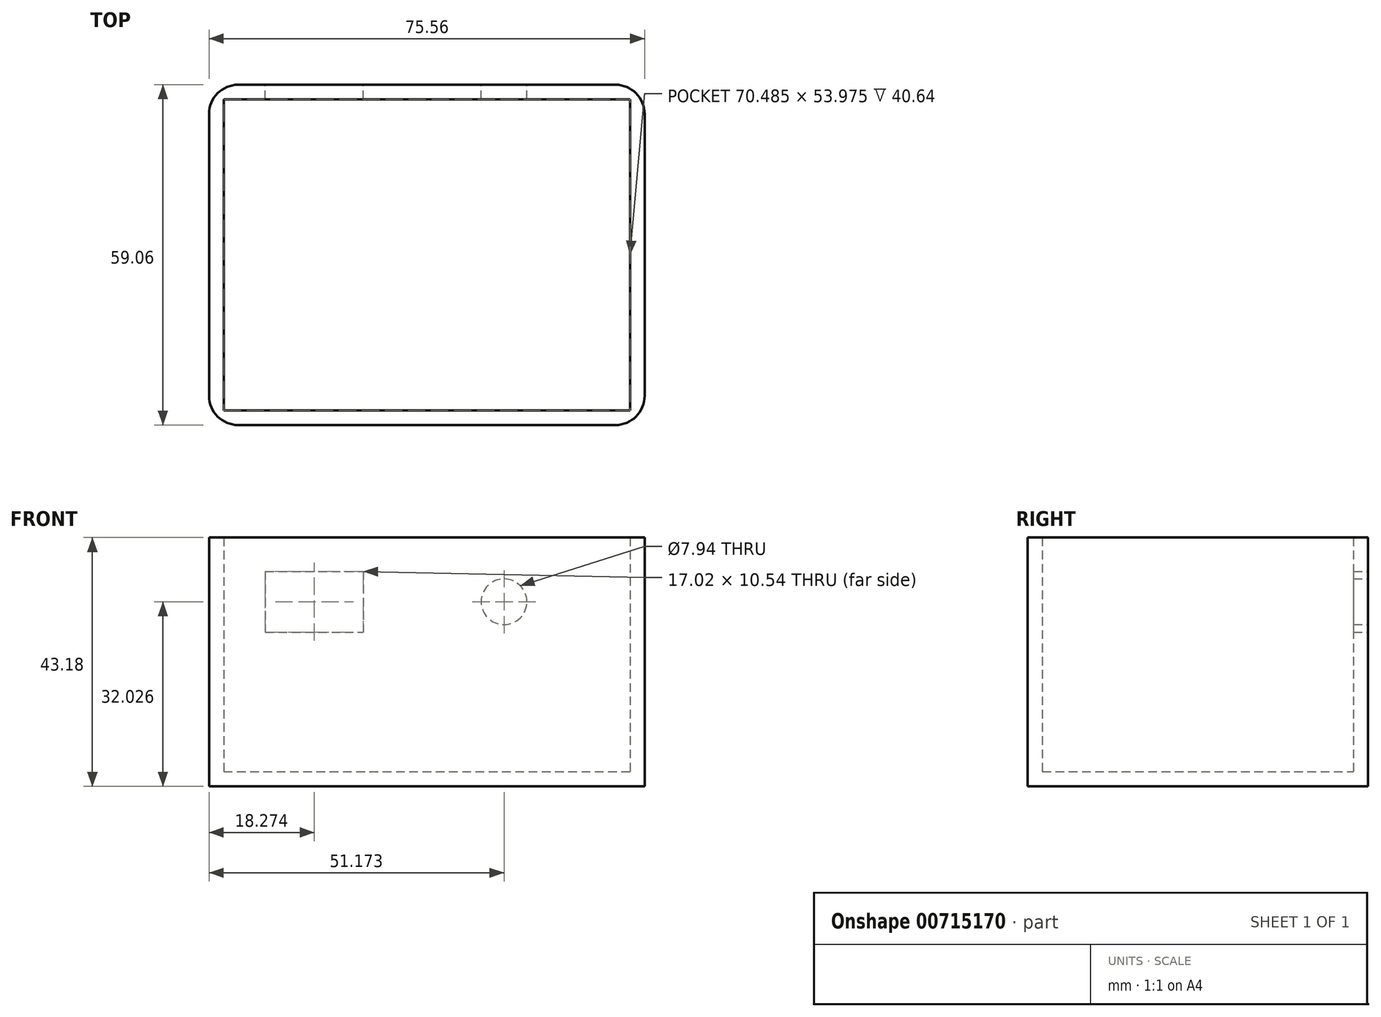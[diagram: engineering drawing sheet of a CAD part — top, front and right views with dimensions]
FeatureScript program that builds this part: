
annotation { "Feature Type Name" : "Feature", "Feature Type Description" : "" }
export const myFeature = defineFeature(function(context is Context, id is Id, definition is map)
    precondition{}
    {
        {
            var Q0;
            Q0=qCreatedBy(makeId("Top.planeOp"),FACE);
            var sketch = newSketch(context, id + "F0", { "sketchPlane" : qUnion([Q0])});
            skLineSegment(sketch, "E0.bottom", {"start": v(-37.78, -29.53) * mm, "end": v(37.78, -29.53) * mm});
            skLineSegment(sketch, "E0.top", {"start": v(-37.78, 29.53) * mm, "end": v(37.78, 29.53) * mm});
            skLineSegment(sketch, "E0.left", {"start": v(-37.78, -29.53) * mm, "end": v(-37.78, 29.53) * mm});
            skLineSegment(sketch, "E0.right", {"start": v(37.78, -29.53) * mm, "end": v(37.78, 29.53) * mm});
            skPoint(sketch, "E0.middle", {"position": v(0, 0) * mm});
            skSolve(sketch);
        }
        {
            var Q0;
            Q0=qSketchRegion(id+"F0",true);
            extrude(context, id + "F1", {"entities" : qUnion([Q0]), "depth" : 43.18 * mm, "offsetDistance" : 25.4 * mm});
        }
        {
            var Q0;
            Q0=makeQuery(id+"F1.opExtrude","CAP_FACE",FACE,{"disambiguationData":[OSD([sQuery(id+"F0.wireOp",EDGE,"E0.bottom"),sQuery(id+"F0.wireOp",EDGE,"E0.top"),sQuery(id+"F0.wireOp",EDGE,"E0.left"),sQuery(id+"F0.wireOp",EDGE,"E0.right")])],"isStart":false});
            shell(context, id + "F2", {"entities" : qUnion([Q0]), "thickness" : 2.54 * mm});
        }
        {
            var Q0;
            Q0=makeQuery(id+"F1.opExtrude","SWEPT_FACE",FACE,{"disambiguationData":[OSD([sQuery(id+"F0.wireOp",EDGE,"E0.top")])]});
            var sketch = newSketch(context, id + "F3", { "sketchPlane" : qUnion([Q0])});
            skLineSegment(sketch, "E1.bottom", {"start": v(28.01, 37.3) * mm, "end": v(11, 37.3) * mm});
            skLineSegment(sketch, "E1.top", {"start": v(28.01, 26.76) * mm, "end": v(11, 26.76) * mm});
            skLineSegment(sketch, "E1.left", {"start": v(28.01, 37.3) * mm, "end": v(28.01, 26.76) * mm});
            skLineSegment(sketch, "E1.right", {"start": v(11, 37.3) * mm, "end": v(11, 26.76) * mm});
            skPoint(sketch, "E1.middle", {"position": v(19.5, 32.03) * mm});
            skSolve(sketch);
        }
        {
            var Q0;
            Q0=qSketchRegion(id+"F3",true);
            extrude(context, id + "F4", {"entities" : qUnion([Q0]), "operationType" : NewBodyOperationType.REMOVE, "oppositeDirection" : true, "depth" : 3.3 * mm, "offsetDistance" : 25.4 * mm});
        }
        {
            var Q0;
            Q0=makeQuery(id+"F1.opExtrude","SWEPT_FACE",FACE,{"disambiguationData":[OSD([sQuery(id+"F0.wireOp",EDGE,"E0.top")])]});
            var sketch = newSketch(context, id + "F5", { "sketchPlane" : qUnion([Q0])});
            skLineSegment(sketch, "E2", {"start": v(-13.4, 43.18) * mm, "end": v(-13.4, 32.03) * mm});
            skLineSegment(sketch, "E3", {"start": v(11, 32.03) * mm, "end": v(-37.78, 32.03) * mm});
            skSolve(sketch);
        }
        {
            var Q0;
            Q0=sQuery(id+"F5.wireOp",VERTEX,"ISpM8A6w-PKEW-MHMS-DoUG-373GydDGFNZQ.end");
            var Q1;
            Q1=sQuery(id+"F5.wireOp",VERTEX,"E2.end");
            var Q2;
            Q2=makeQuery(id+"F1.opExtrude","SWEPT_BODY",BODY,{"disambiguationData":[OSD([sQuery(id+"F0.wireOp",EDGE,"E0.bottom"),sQuery(id+"F0.wireOp",EDGE,"E0.top"),sQuery(id+"F0.wireOp",EDGE,"E0.left"),sQuery(id+"F0.wireOp",EDGE,"E0.right")])]});
            hole(context, id + "F6", {"style" : HoleStyle.SIMPLE, "endStyle" : HoleEndStyle.BLIND, "holeDiameter" : 7.94 * mm, "majorDiameter" : 6.35 * mm, "holeDepth" : 12.7 * mm, "isTappedThrough" : true, "tappedDepth" : 12.7 * mm, "tapClearance" : 3, "locations" : qUnion([Q0, Q1]), "scope" : qUnion([Q2])});
        }
        {
            var Q0;
            Q0=makeQuery(id+"F1.opExtrude","SWEPT_EDGE",EDGE,{"disambiguationData":[OSD([sQuery(id+"F0.wireOp",EDGE,"E0.bottom"),sQuery(id+"F0.wireOp",EDGE,"E0.left")])]});
            var Q1;
            Q1=makeQuery(id+"F1.opExtrude","SWEPT_EDGE",EDGE,{"disambiguationData":[OSD([sQuery(id+"F0.wireOp",EDGE,"E0.bottom"),sQuery(id+"F0.wireOp",EDGE,"E0.right")])]});
            var Q2;
            Q2=makeQuery(id+"F1.opExtrude","SWEPT_EDGE",EDGE,{"disambiguationData":[OSD([sQuery(id+"F0.wireOp",EDGE,"E0.top"),sQuery(id+"F0.wireOp",EDGE,"E0.right")])]});
            var Q3;
            Q3=makeQuery(id+"F1.opExtrude","SWEPT_EDGE",EDGE,{"disambiguationData":[OSD([sQuery(id+"F0.wireOp",EDGE,"E0.top"),sQuery(id+"F0.wireOp",EDGE,"E0.left")])]});
            fillet(context, id + "F7", {"entities" : qUnion([Q0, Q1, Q2, Q3]), "radius" : 5.08 * mm, "tangentPropagation" : true, "allowEdgeOverflow" : false});
        }
    });
